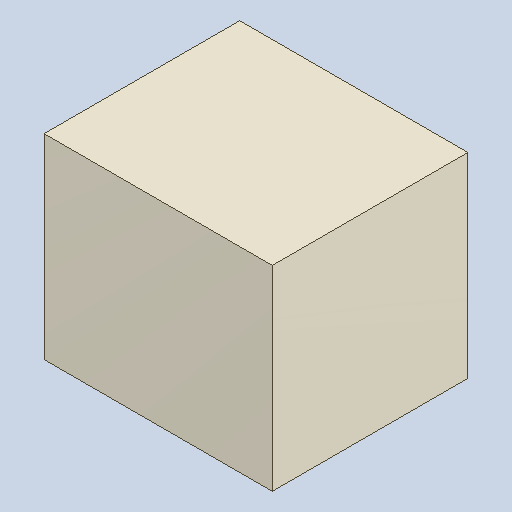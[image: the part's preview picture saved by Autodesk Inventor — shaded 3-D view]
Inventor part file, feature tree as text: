
AUTODESK INVENTOR PART (.ipt)
format: ipt  version: 2023.4 (Build 274418000, 418)  size: 82,432 bytes
history: native  units: mm
features: extrude x1
ambient origin geometry x8: Origin, YZ Plane, XZ Plane, XY Plane, X Axis, Y Axis, Z Axis, Center Point
bodies: Solid1 (feature_tree)
feature tree (1):
  extrude  "Extruded_13"  [1 undecoded]
note: 1 required parameter value undecoded (feature->parameter linkage not recoverable at this tier; creation-order binding heuristic only, values carry confidence <= 0.55)
